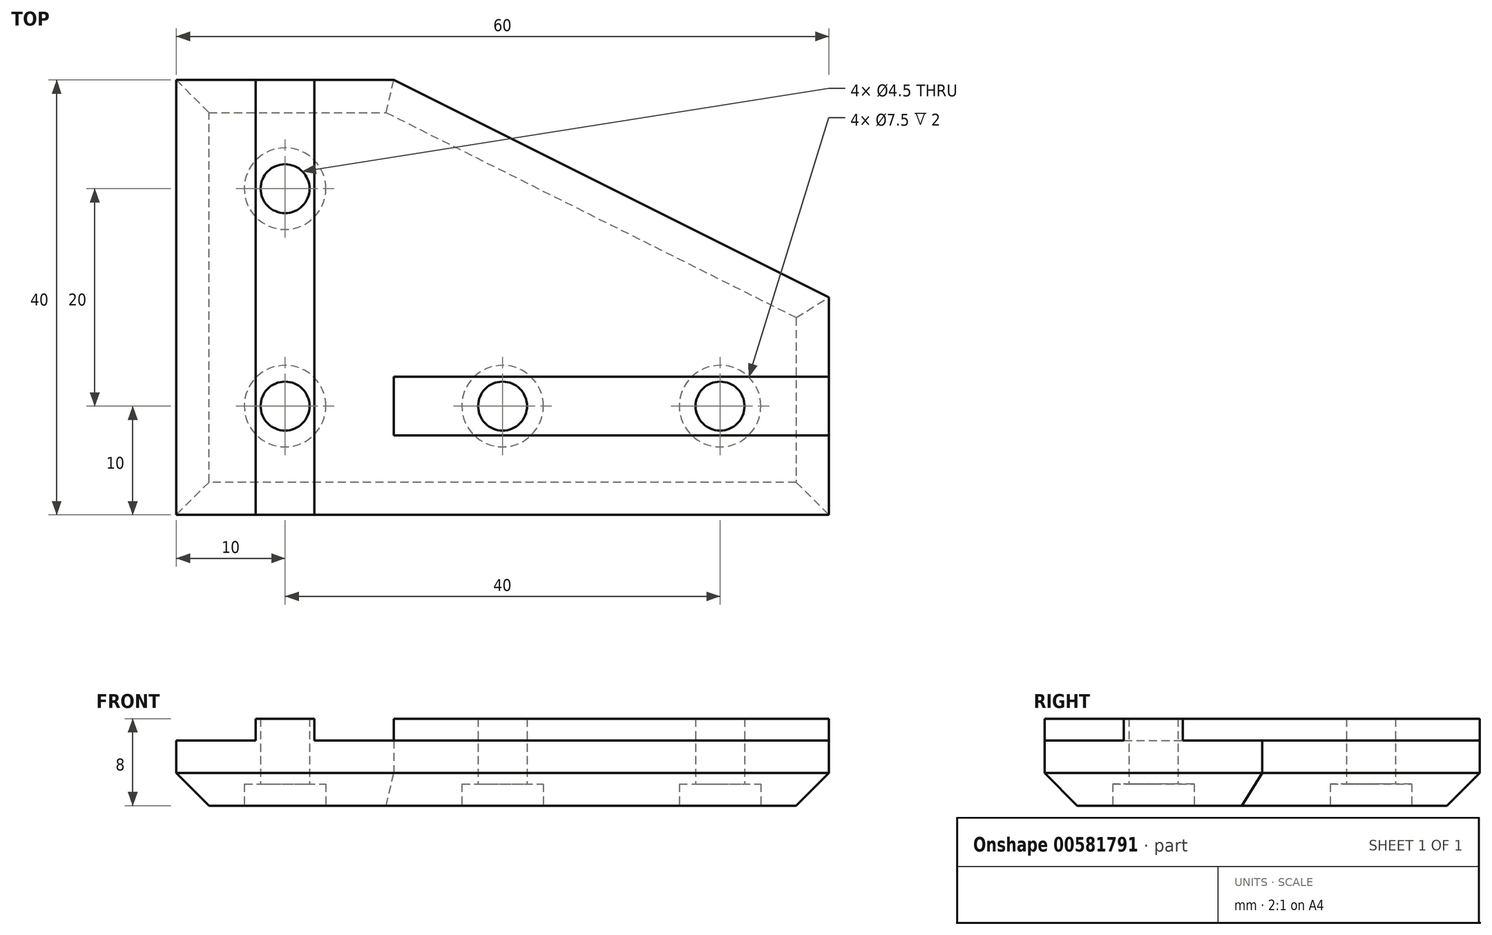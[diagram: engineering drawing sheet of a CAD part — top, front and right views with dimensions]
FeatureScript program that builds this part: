
annotation { "Feature Type Name" : "Feature", "Feature Type Description" : "" }
export const myFeature = defineFeature(function(context is Context, id is Id, definition is map)
    precondition{}
    {
        {
            var Q0;
            Q0=qCreatedBy(makeId("Top.planeOp"),FACE);
            var sketch = newSketch(context, id + "F0", { "sketchPlane" : qUnion([Q0])});
            skLineSegment(sketch, "E0", {"start": v(0, 0) * mm, "end": v(0, 40) * mm});
            skLineSegment(sketch, "E1", {"start": v(0, 40) * mm, "end": v(20, 40) * mm});
            skLineSegment(sketch, "E2", {"start": v(20, 40) * mm, "end": v(20, 20) * mm, "construction": true});
            skLineSegment(sketch, "E3", {"start": v(20, 20) * mm, "end": v(60, 20) * mm, "construction": true});
            skLineSegment(sketch, "E4", {"start": v(60, 20) * mm, "end": v(60, 0) * mm});
            skLineSegment(sketch, "E5", {"start": v(60, 0) * mm, "end": v(0, 0) * mm});
            skLineSegment(sketch, "E6", {"start": v(20, 40) * mm, "end": v(60, 20) * mm});
            skSolve(sketch);
        }
        {
            var Q0;
            Q0=qSketchRegion(id+"F0",true);
            extrude(context, id + "F1", {"entities" : qUnion([Q0]), "depth" : 6 * mm});
        }
        {
            var Q0;
            Q0=makeQuery(id+"F1.opExtrude","CAP_FACE",FACE,{"disambiguationData":[OSD([sQuery(id+"F0.wireOp",EDGE,"E0"),sQuery(id+"F0.wireOp",EDGE,"E1"),sQuery(id+"F0.wireOp",EDGE,"E2"),sQuery(id+"F0.wireOp",EDGE,"E3"),sQuery(id+"F0.wireOp",EDGE,"E4"),sQuery(id+"F0.wireOp",EDGE,"E5")])],"isStart":false});
            var sketch = newSketch(context, id + "F2", { "sketchPlane" : qUnion([Q0])});
            skLineSegment(sketch, "E7", {"start": v(7.3, 40) * mm, "end": v(12.71, 40) * mm});
            skLineSegment(sketch, "E8", {"start": v(12.71, 40) * mm, "end": v(12.71, 0) * mm});
            skLineSegment(sketch, "E9", {"start": v(12.71, 0) * mm, "end": v(10, 0) * mm});
            skPoint(sketch, "E9.endSnap0", {"position": v(10, 40) * mm});
            skLineSegment(sketch, "E10", {"start": v(10, 0) * mm, "end": v(7.3, 0) * mm});
            skLineSegment(sketch, "E11", {"start": v(7.3, 0) * mm, "end": v(7.3, 40) * mm});
            skLineSegment(sketch, "E12", {"start": v(60, 12.7) * mm, "end": v(60, 7.3) * mm});
            skLineSegment(sketch, "E13", {"start": v(60, 7.3) * mm, "end": v(20, 7.3) * mm});
            skLineSegment(sketch, "E14", {"start": v(20, 7.3) * mm, "end": v(20, 10) * mm});
            skPoint(sketch, "E14.endSnap0", {"position": v(60, 10) * mm});
            skLineSegment(sketch, "E15", {"start": v(20, 10) * mm, "end": v(20, 12.71) * mm});
            skLineSegment(sketch, "E16", {"start": v(20, 12.71) * mm, "end": v(60, 12.71) * mm});
            skSolve(sketch);
        }
        {
            var Q0;
            Q0=qSketchRegion(id+"F2",true);
            extrude(context, id + "F3", {"entities" : qUnion([Q0]), "operationType" : NewBodyOperationType.ADD, "depth" : 2 * mm});
        }
        {
            var Q0;
            Q0=makeQuery(id+"F1.opExtrude","CAP_FACE",FACE,{"disambiguationData":[OSD([sQuery(id+"F0.wireOp",EDGE,"E0"),sQuery(id+"F0.wireOp",EDGE,"E1"),sQuery(id+"F0.wireOp",EDGE,"E2"),sQuery(id+"F0.wireOp",EDGE,"E3"),sQuery(id+"F0.wireOp",EDGE,"E4"),sQuery(id+"F0.wireOp",EDGE,"E5")])],"isStart":true});
            var sketch = newSketch(context, id + "F4", { "sketchPlane" : qUnion([Q0])});
            skCircle(sketch, "E17", {"center": v(10, -10) * mm, "radius": 2.25 * mm});
            skCircle(sketch, "E18", {"center": v(50, -10) * mm, "radius": 2.25 * mm});
            skCircle(sketch, "E19", {"center": v(10, -30) * mm, "radius": 2.25 * mm});
            skCircle(sketch, "E20", {"center": v(30, -10) * mm, "radius": 2.25 * mm});
            skSolve(sketch);
        }
        {
            var Q0;
            Q0=qSketchRegion(id+"F4",true);
            extrude(context, id + "F5", {"entities" : qUnion([Q0]), "operationType" : NewBodyOperationType.REMOVE, "endBound" : BoundingType.THROUGH_ALL, "oppositeDirection" : true, "depth" : 25 * mm});
        }
        {
            var Q0;
            Q0=makeQuery(id+"F1.opExtrude","CAP_FACE",FACE,{"disambiguationData":[OSD([sQuery(id+"F0.wireOp",EDGE,"E0"),sQuery(id+"F0.wireOp",EDGE,"E1"),sQuery(id+"F0.wireOp",EDGE,"E2"),sQuery(id+"F0.wireOp",EDGE,"E3"),sQuery(id+"F0.wireOp",EDGE,"E4"),sQuery(id+"F0.wireOp",EDGE,"E5")])],"isStart":true});
            var sketch = newSketch(context, id + "F6", { "sketchPlane" : qUnion([Q0])});
            skCircle(sketch, "E21", {"center": v(10, -10) * mm, "radius": 3.75 * mm});
            skCircle(sketch, "E22", {"center": v(30, -10) * mm, "radius": 3.75 * mm});
            skCircle(sketch, "E23", {"center": v(50, -10) * mm, "radius": 3.75 * mm});
            skCircle(sketch, "E24", {"center": v(10, -30) * mm, "radius": 3.75 * mm});
            skSolve(sketch);
        }
        {
            var Q0;
            Q0=qSketchRegion(id+"F6",true);
            extrude(context, id + "F7", {"entities" : qUnion([Q0]), "operationType" : NewBodyOperationType.REMOVE, "oppositeDirection" : true, "depth" : 2 * mm});
        }
        {
            var Q0;
            Q0=makeQuery(id+"F1.opExtrude","CAP_EDGE",EDGE,{"disambiguationData":[OSD([sQuery(id+"F0.wireOp",EDGE,"E5")])],"isStart":true});
            var Q1;
            Q1=makeQuery(id+"F1.opExtrude","CAP_EDGE",EDGE,{"disambiguationData":[OSD([sQuery(id+"F0.wireOp",EDGE,"E0")])],"isStart":true});
            var Q2;
            Q2=makeQuery(id+"F1.opExtrude","CAP_EDGE",EDGE,{"disambiguationData":[OSD([sQuery(id+"F0.wireOp",EDGE,"E2")])],"isStart":true});
            var Q3;
            Q3=makeQuery(id+"F1.opExtrude","CAP_EDGE",EDGE,{"disambiguationData":[OSD([sQuery(id+"F0.wireOp",EDGE,"E3")])],"isStart":true});
            var Q4;
            Q4=makeQuery(id+"F1.opExtrude","CAP_EDGE",EDGE,{"disambiguationData":[OSD([sQuery(id+"F0.wireOp",EDGE,"E4")])],"isStart":true});
            var Q5;
            Q5=makeQuery(id+"F1.opExtrude","CAP_EDGE",EDGE,{"disambiguationData":[OSD([sQuery(id+"F0.wireOp",EDGE,"E1")])],"isStart":true});
            var Q6;
            Q6=makeQuery(id+"F1.opExtrude","CAP_EDGE",EDGE,{"disambiguationData":[OSD([sQuery(id+"F0.wireOp",EDGE,"E6")])],"isStart":true});
            chamfer(context, id + "F8", {"entities" : qUnion([Q0, Q1, Q2, Q3, Q4, Q5, Q6]), "width" : 3 * mm, "tangentPropagation" : true});
        }
    });
